# Revit family: I-vent 500-1500 E W
name_source: partatom
category: Оборудование
units: mm (PartAtom-declared; Revit-internal decimal feet)

## family parameters
Всегда вертикально = Да
Классификация = Нет
На основе рабочей плоскости = Нет
Общий = Нет
При загрузке вырезать с полостями = Нет
Размер круглого соединителя = Использовать диаметр
Тип детали = Нормальный
Точка расчета площади = Нет

## types (8) — shared parameters
ADSK_Единица измерения = шт.
ADSK_Завод-изготовитель = ООО «Турков»
ADSK_Наименование = Приточная установка с высокой фильтрацией воздуха с нагревателем I-VENT
ВВ_толщ = 30 мм
КА_высота = 190 мм
КА_х = 45 мм
КА_ширина = 173 мм

## per-type parameters (varying)
| type | A1 длина | ADSK_Количество фаз | ADSK_Марка | ADSK_Масса | ADSK_Напряжение | ADSK_Номинальная мощность | ADSK_Свободный напор воздуха | ADSK_Ток | B1 глубина | C1 высота | ВВ_Dn | ВВ_У | ВП | КА_толщина | Кол-во вентиляторов | СЗ | СУ подкл | Тип нагревателя | Угол УГО |
| I-Vent 500 E v2 | 1331 мм | 1 | I-Vent 500 E | 37 | 220 В | 4820 Вт | 333.0 Па | 22 А | 340 мм | 556 мм | 200 мм | 165 мм | Нет | 105 мм | 1 | 320 мм | 610 мм | ТЭН | 16.70° |
| I-Vent 500 E v3 | 1331 мм | 1 | I-Vent 500 E | 37 | 220 В | 4995 Вт | 333.0 Па | 22 А | 340 мм | 556 мм | 200 мм | 165 мм | Нет | 105 мм | 2 | 320 мм | 610 мм | Керамический | 16.70° |
| I-Vent 1000 E | 1825 мм | 3 | I-Vent 1000 E | 48 | 380 В | 12375 Вт | 149.0 Па | 19 А | 390 мм | 660 мм | 250 мм | 192 мм | Нет | 75 мм | 1 | 400 мм | 610 мм | ТЭН | 13.50° |
| I-Vent 1500 E | 1825 мм | 3 | I-Vent 1500 E | 76 | 380 В | 18520 Вт | 167.0 Па | 28 А | 440 мм | 660 мм | 315 мм | 217 мм | Нет | 75 мм | 1 | 500 мм | 19 мм | ТЭН | 10.78° |
| I-Vent 500 W v2 | 1331 мм | 1 | I-Vent 500 W | 37 | 220 В | 391 Вт | 374.0 Па | 2 А | 340 мм | 556 мм | 200 мм | 165 мм | Нет | 105 мм | 1 | 320 мм | 610 мм | Водяной | 16.70° |
| I-Vent 500 W v3 | 1331 мм | 1 | I-Vent 500 W | 37 | 220 В | 566 Вт | 374.0 Па | 2 А | 340 мм | 556 мм | 200 мм | 165 мм | Да | 105 мм | 2 | 320 мм | 19 мм | Водяной | 16.70° |
| I-Vent 1500 W | 1825 мм | 1 | I-Vent 1500 W | 76 | 220 В | 571 Вт | 165.0 Па | 3 А | 440 мм | 660 мм | 315 мм | 217 мм | Да | 75 мм | 1 | 500 мм | 610 мм | Водяной | 10.78° |
| I-Vent 1000 W | 1825 мм | 1 | I-Vent 1000 W | 48 | 220 В | 446 Вт | 147.0 Па | 2 А | 390 мм | 660 мм | 250 мм | 192 мм | Да | 75 мм | 1 | 400 мм | 610 мм | Водяной | 13.50° |

## geometry (parser evidence)
native form markers: Sweep x4
no freeform markers — native parametric forms only
